# Revit family: BasinMixer_Countertop_SiphonOperated_Vitra_XLineSeries_A42325
name_source: partatom
category: Plumbing Fixtures
revit_build: Autodesk Revit 2017 (Build: 20160225_1515(x64)
units: mm (PartAtom-declared; Revit-internal decimal feet)

## family parameters
Cut with Voids When Loaded = No
Host = Face
OmniClass Number = 23.45.55.17
OmniClass Title = Mixing Faucets
Part Type = Normal
Room Calculation Point = No
Round Connector Dimension = Use Diameter
Shared = Yes

## types (9) — shared parameters
BIMobject category = Taps & Mixers
CW Connection = Yes
Default Elevation = 850 mm  [stored 2.78871 ft]
Depth(mm) = 195 mm
Description = X-Line Basin Mixer
Design country = Turkey
HW Connection = Yes
Height(mm) = 190 mm
Hot Water Supply (max.) = 80 °C
Hot Water temperature, factory set to = 38 °C
IFC Classification = Sanitary Terminal
Main Material = Brass
Manufacturer = Vitra
Manufacturer name = Vitra
Masterformat 2014 Code = 22 40 00
Masterformat 2014 Description = Plumbing Fixtures
Min. flow pressure of = 0.5 bar
MountingType = Countertop
NBS Referans Code = 45-35-70/371
NBS Referans Description = Water supply fittings for wash basins and troughs
Nominal height = 0.000
Nominal width = 0.000
Number Of Connections = 2 mm  [stored 0.00656168 ft]
OmniClass Code = 23.45.55.17
OmniClass Description = Mixing Faucets
Product Properties = Extra Water Saving
Product Type = Basin Mixer
Product certification = https://vitraglobal.com
Product family = X-Line
Product group = X-Line Basin Mixer
Range of Hot Water Supply = 5 - 65 °C
Range of flow pressure = 1 - 5 bar
Test Pressure = 16 bar
UNSPSC Code = 301815
URL = https://vitraglobal.com
Uniclass 1.4 Code = L725111
Uniclass 1.4 Description = Mixer taps
Uniclass 2.0 Code = Pr_40_30_96_98
Uniclass 2.0 Description = Washbasin Tap
Uniclass 2015 Code = Pr_40_20_87_98
Uniclass 2015 Name = Washbasin Tap
Uniformat II Code = 22 40 00
Uniformat II Description = Plumbing Fixture
Weight Net (kg) = 2.190
Width(mm) = 50 mm  [stored 0.164042 ft]
Youtube = https://www.youtube.com
zero-valued in all types: Cost

## per-type parameters (varying)
| type | Article No. (default) | Brand | Coating Material | Color | Connection Diameter (mm) | Flow Rate(L/min. - 3 bar) | Installation instructions | Model | Product Guid | Product SKU | Product data url | Technical description | Warranty Period (Year) |
| BasinMixer-XLineSeries-A42325 | A42325 | Artema | Chrome | Chrome | 10 mm  [stored 0.0328084 ft] | 5 L/min. |  | A42325 |  | A42325 | https://www.vitra.com.tr | https://www.vitra.com.tr | 10 Years |
| BasinMixer-XLineSeries-A4232523 | A4232523 | Artema | Gold | Gold | 10 mm  [stored 0.0328084 ft] | 5 L/min. |  | A4232523 |  | A4232523 | https://www.vitra.com.tr | https://www.vitra.com.tr | 10 Years |
| BasinMixer-XLineSeries-A42325EXP | A42325EXP | Vitra | Chrome | Chrome | 10 mm  [stored 0.0328084 ft] | 3 L/min. | https://cdn.vitra.com.tr | A42325EXP | https://cdn.vitra.com.tr | A42325EXP | https://www.vitraglobal.com | https://www.vitraglobal.com | 7 Years |
| BasinMixer-XLineSeries-A42325IND | A42325IND | Vitra | Chrome | Chrome | 15 mm  [stored 0.0492126 ft] | 3 L/min. | https://cdn.vitra.com.tr | A42325IND | https://cdn.vitra.com.tr | A42325IND | https://www.vitraglobal.com | https://www.vitraglobal.com | 7 Years |
| BasinMixer-XLineSeries-A4232523EXP | A4232523EXP | Vitra | Chrome | Chrome | 10 mm  [stored 0.0328084 ft] | 3 L/min. | https://cdn.vitra.com.tr | A4232523EXP | https://cdn.vitra.com.tr | A4232523EXP | https://www.vitraglobal.com | https://www.vitraglobal.com | 7 Years |
| BasinMixer-XLineSeries-A42325VUK | A42325VUK | Vitra | Chrome | Chrome | 10 mm  [stored 0.0328084 ft] | 3 L/min. | https://cdn.vitra.com.tr | A42325VUK | https://cdn.vitra.com.tr | A42325VUK | https://www.vitraglobal.com | https://www.vitraglobal.com | 7 Years |
| BasinMixer-XLineSeries-A42325ENG | A42325ENG | Vitra | Chrome | Chrome | 10 mm  [stored 0.0328084 ft] | 3 L/min. | https://cdn.vitra.com.tr | A42325ENG | https://cdn.vitra.com.tr | A42325ENG | https://www.vitraglobal.com | https://www.vitraglobal.com | 7 Years |
| BasinMixer-XLineSeries-A42325EKF | A42325EKF | Vitra | Chrome | Chrome | 10 mm  [stored 0.0328084 ft] | 3 L/min. | https://cdn.vitra.com.tr | A42325EKF | https://cdn.vitra.com.tr | A42325EKF | https://www.vitraglobal.com | https://www.vitraglobal.com | 7 Years |
| BasinMixer-XLineSeries-A42325ENGX | A42325ENGX | Vitra | Chrome | Chrome | 10 mm  [stored 0.0328084 ft] | 3 L/min. | https://cdn.vitra.com.tr | A42325ENGX | https://cdn.vitra.com.tr | A42325ENGX | https://www.vitraglobal.com | https://www.vitraglobal.com | 7 Years |

note: [stored X ft] marks values corroborated as IEEE doubles in the binary element streams (Revit-internal decimal feet)

## geometry (parser evidence)
native form markers: Sweep x3
no freeform markers — native parametric forms only
